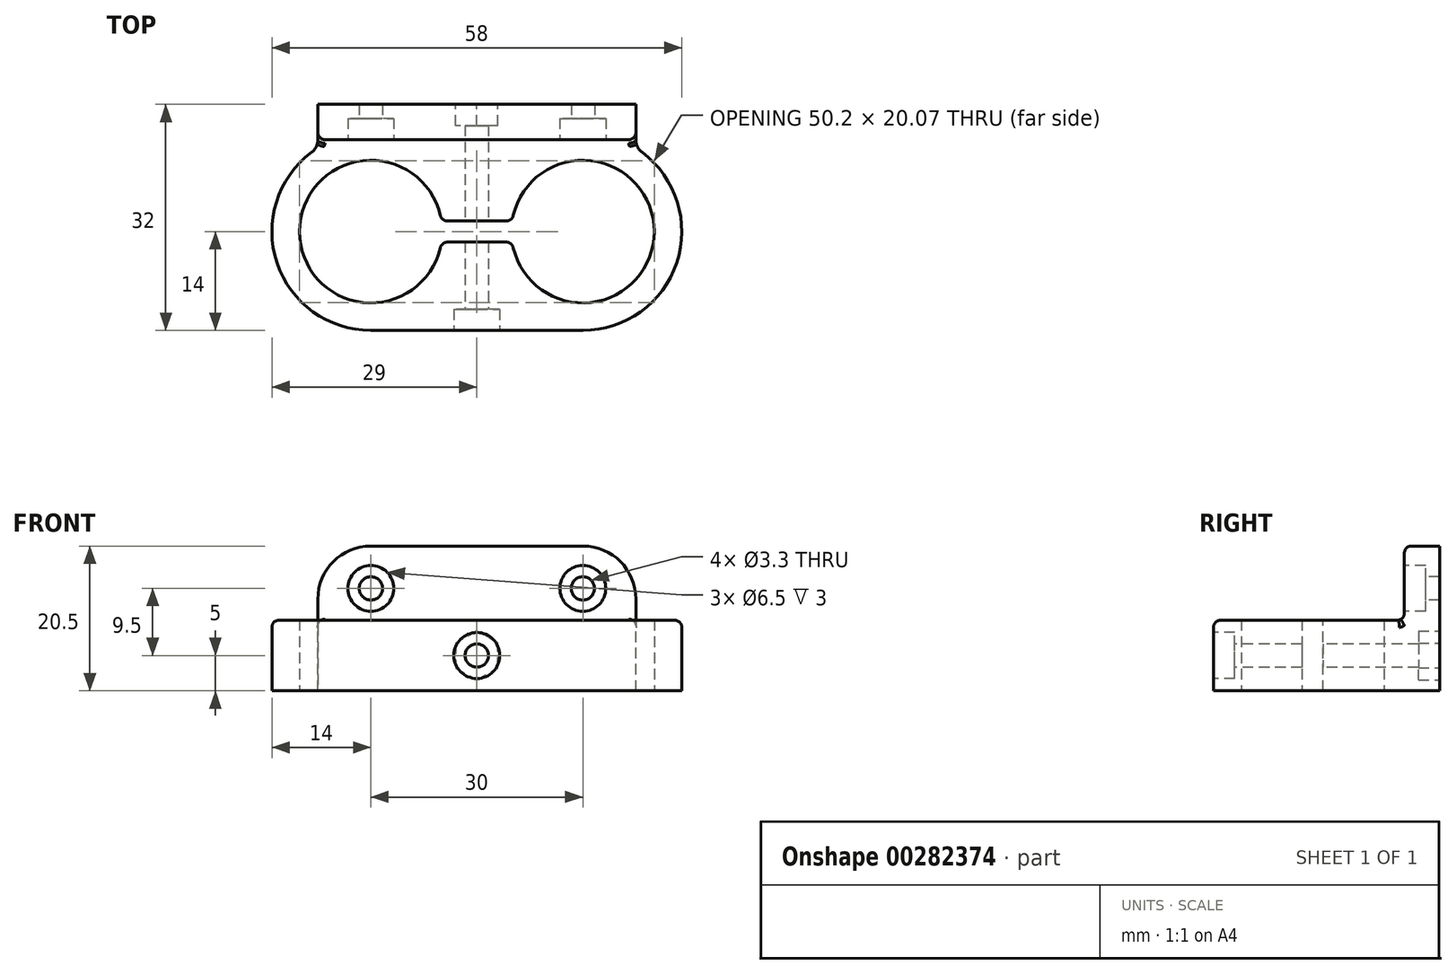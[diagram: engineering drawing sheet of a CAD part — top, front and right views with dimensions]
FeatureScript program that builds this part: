
annotation { "Feature Type Name" : "Feature", "Feature Type Description" : "" }
export const myFeature = defineFeature(function(context is Context, id is Id, definition is map)
    precondition{}
    {
        {
            var Q0;
            Q0=qCreatedBy(makeId("Front.planeOp"),FACE);
            var sketch = newSketch(context, id + "F0", { "sketchPlane" : qUnion([Q0])});
            skLineSegment(sketch, "E0.bottom", {"start": v(0, 0) * mm, "end": v(45, 0) * mm});
            skLineSegment(sketch, "E0.top", {"start": v(7.5, 20.5) * mm, "end": v(37.5, 20.5) * mm});
            skLineSegment(sketch, "E0.left", {"start": v(0, 0) * mm, "end": v(0, 13) * mm});
            skLineSegment(sketch, "E0.right", {"start": v(45, 0) * mm, "end": v(45, 13) * mm});
            skPoint(sketch, "E1.visualSharp", {"position": v(0, 20.5) * mm});
            skArc(sketch, "E1.filletArc", {"start": v(7.5, 20.5) * mm, "mid": v(2.2, 18.3) * mm, "end": v(0, 13) * mm});
            skPoint(sketch, "E2.visualSharp", {"position": v(45, 20.5) * mm});
            skArc(sketch, "E2.filletArc", {"start": v(45, 13) * mm, "mid": v(42.8, 18.3) * mm, "end": v(37.5, 20.5) * mm});
            skSolve(sketch);
        }
        {
            var Q0;
            Q0=qSketchRegion(id+"F0",true);
            extrude(context, id + "F1", {"entities" : qUnion([Q0]), "depth" : 5 * mm});
        }
        {
            var Q0;
            Q0=makeQuery(id+"F1.opExtrude","CAP_FACE",FACE,{"disambiguationData":[OSD([sQuery(id+"F0.wireOp",EDGE,"E0.bottom"),sQuery(id+"F0.wireOp",EDGE,"E0.top"),sQuery(id+"F0.wireOp",EDGE,"E0.left"),sQuery(id+"F0.wireOp",EDGE,"E0.right")])],"isStart":false});
            var sketch = newSketch(context, id + "F2", { "sketchPlane" : qUnion([Q0])});
            skLineSegment(sketch, "E3", {"start": v(0, 14.5) * mm, "end": v(45, 14.5) * mm, "construction": true});
            skLineSegment(sketch, "E4", {"start": v(22.5, 20.5) * mm, "end": v(22.5, 14.5) * mm, "construction": true});
            skPoint(sketch, "E5", {"position": v(7.5, 14.5) * mm});
            skPoint(sketch, "E6", {"position": v(37.5, 14.5) * mm});
            skSolve(sketch);
        }
        {
            var Q0;
            Q0=sQuery(id+"F2.wireOp",VERTEX,"E5");
            var Q1;
            Q1=sQuery(id+"F2.wireOp",VERTEX,"E6");
            var Q2;
            Q2=makeQuery(id+"F1.opExtrude","SWEPT_BODY",BODY,{"disambiguationData":[OSD([sQuery(id+"F0.wireOp",EDGE,"E0.bottom"),sQuery(id+"F0.wireOp",EDGE,"E0.top"),sQuery(id+"F0.wireOp",EDGE,"E0.left"),sQuery(id+"F0.wireOp",EDGE,"E0.right")])]});
            hole(context, id + "F3", {"style" : HoleStyle.C_BORE, "endStyle" : HoleEndStyle.THROUGH, "standardTappedOrClearance" : lookupTablePath({ "standard" : "ISO", "fit" : "Normal", "size" : "M3", "type" : "Clearance" }), "standardBlindInLast" : lookupTablePath({ "fit" : "Standard", "standard" : "ISO", "size" : "M3", "type" : "Clearance" }), "holeDiameter" : 3.3 * mm, "cBoreDiameter" : 6.5 * mm, "cBoreDepth" : 3 * mm, "tappedDepth" : 3 * mm, "tapClearance" : 3, "startFromSketch" : true, "locations" : qUnion([Q0, Q1]), "scope" : qUnion([Q2])});
        }
        {
            var Q0;
            Q0=qCreatedBy(makeId("Top.planeOp"),FACE);
            var sketch = newSketch(context, id + "F4", { "sketchPlane" : qUnion([Q0])});
            skLineSegment(sketch, "E7.bottom", {"start": v(0, 0) * mm, "end": v(45, 0) * mm});
            skLineSegment(sketch, "E7.top", {"start": v(7.5, -32) * mm, "end": v(37.5, -32) * mm});
            skLineSegment(sketch, "E7.left", {"start": v(0, 0) * mm, "end": v(0, -6.18) * mm});
            skLineSegment(sketch, "E7.right", {"start": v(45, 0) * mm, "end": v(45, -6.18) * mm});
            skLineSegment(sketch, "E8", {"start": v(0, -18) * mm, "end": v(45, -18) * mm, "construction": true});
            skLineSegment(sketch, "E9", {"start": v(22.5, -18) * mm, "end": v(22.5, -32) * mm, "construction": true});
            skArc(sketch, "E10", {"start": v(17.49, -16.5) * mm, "mid": v(-2.6, -18) * mm, "end": v(17.49, -19.5) * mm});
            skArc(sketch, "E11", {"start": v(27.51, -19.5) * mm, "mid": v(47.6, -18) * mm, "end": v(27.51, -16.5) * mm});
            skArc(sketch, "E12", {"start": v(37.5, -32) * mm, "mid": v(50.94, -21.9) * mm, "end": v(45, -6.18) * mm});
            skArc(sketch, "E13", {"start": v(0, -6.18) * mm, "mid": v(-5.94, -21.9) * mm, "end": v(7.5, -32) * mm});
            skLineSegment(sketch, "E14.trimOffspring", {"start": v(0, -18) * mm, "end": v(0, -32) * mm, "construction": true});
            skLineSegment(sketch, "E15.trimOffspring", {"start": v(45, -18) * mm, "end": v(45, -32) * mm, "construction": true});
            skLineSegment(sketch, "E16.0", {"start": v(17.49, -19.5) * mm, "end": v(27.51, -19.5) * mm});
            skLineSegment(sketch, "E17.0", {"start": v(17.49, -16.5) * mm, "end": v(27.51, -16.5) * mm});
            skSolve(sketch);
        }
        {
            var Q0;
            Q0=qSketchRegion(id+"F4",true);
            extrude(context, id + "F5", {"entities" : qUnion([Q0]), "operationType" : NewBodyOperationType.ADD, "depth" : 10 * mm});
        }
        {
            var Q0;
            Q0=makeQuery(id+"F5.opExtrude","SWEPT_FACE",FACE,{"disambiguationData":[OSD([sQuery(id+"F4.wireOp",EDGE,"E7.top")])]});
            var sketch = newSketch(context, id + "F6", { "sketchPlane" : qUnion([Q0])});
            skLineSegment(sketch, "E18", {"start": v(7.5, 5) * mm, "end": v(37.5, 5) * mm, "construction": true});
            skPoint(sketch, "E19", {"position": v(22.5, 5) * mm});
            skSolve(sketch);
        }
        {
            var Q0;
            Q0=sQuery(id+"F6.wireOp",VERTEX,"E19");
            var Q1;
            Q1=makeQuery(id+"F1.opExtrude","SWEPT_BODY",BODY,{"disambiguationData":[OSD([sQuery(id+"F0.wireOp",EDGE,"E0.bottom"),sQuery(id+"F0.wireOp",EDGE,"E0.top"),sQuery(id+"F0.wireOp",EDGE,"E0.left"),sQuery(id+"F0.wireOp",EDGE,"E0.right"),sQuery(id+"F0.wireOp",EDGE,"E1.filletArc"),sQuery(id+"F0.wireOp",EDGE,"E2.filletArc")])]});
            hole(context, id + "F7", {"style" : HoleStyle.C_BORE, "endStyle" : HoleEndStyle.THROUGH, "standardTappedOrClearance" : lookupTablePath({ "standard" : "ISO", "fit" : "Normal", "size" : "M3", "type" : "Clearance" }), "standardBlindInLast" : lookupTablePath({ "fit" : "Standard", "standard" : "ISO", "size" : "M3", "type" : "Clearance" }), "holeDiameter" : 3.3 * mm, "cBoreDiameter" : 6.5 * mm, "cBoreDepth" : 3 * mm, "tappedDepth" : 3 * mm, "tapClearance" : 3, "startFromSketch" : true, "locations" : qUnion([Q0]), "scope" : qUnion([Q1])});
        }
        {
            var Q0;
            Q0=makeQuery(id+"F1.opExtrude","CAP_FACE",FACE,{"disambiguationData":[OSD([sQuery(id+"F0.wireOp",EDGE,"E0.bottom"),sQuery(id+"F0.wireOp",EDGE,"E0.top"),sQuery(id+"F0.wireOp",EDGE,"E0.left"),sQuery(id+"F0.wireOp",EDGE,"E0.right"),sQuery(id+"F0.wireOp",EDGE,"E1.filletArc"),sQuery(id+"F0.wireOp",EDGE,"E2.filletArc")])],"isStart":true});
            var sketch = newSketch(context, id + "F8", { "sketchPlane" : qUnion([Q0])});
            skCircle(sketch, "E20.cCircle", {"center": v(-22.5, 5) * mm, "radius": 3 * mm, "construction": true});
            skLineSegment(sketch, "E20.0", {"start": v(-19.5, 6.73) * mm, "end": v(-19.5, 3.27) * mm});
            skLineSegment(sketch, "E20.1", {"start": v(-19.5, 3.27) * mm, "end": v(-22.5, 1.54) * mm});
            skLineSegment(sketch, "E20.2", {"start": v(-22.5, 1.54) * mm, "end": v(-25.5, 3.27) * mm});
            skLineSegment(sketch, "E20.3", {"start": v(-25.5, 3.27) * mm, "end": v(-25.5, 6.73) * mm});
            skLineSegment(sketch, "E20.4", {"start": v(-25.5, 6.73) * mm, "end": v(-22.5, 8.46) * mm});
            skLineSegment(sketch, "E20.5", {"start": v(-22.5, 8.46) * mm, "end": v(-19.5, 6.73) * mm});
            skPoint(sketch, "E20.0.midPoint", {"position": v(-19.5, 5) * mm});
            skSolve(sketch);
        }
        {
            var Q0;
            Q0=qSketchRegion(id+"F8",true);
            extrude(context, id + "F9", {"entities" : qUnion([Q0]), "operationType" : NewBodyOperationType.REMOVE, "oppositeDirection" : true, "depth" : 3 * mm});
        }
        {
            var Q0;
            Q0=makeQuery(id+"F5.opExtrude","SWEPT_EDGE",EDGE,{"disambiguationData":[OSD([sQuery(id+"F4.wireOp",EDGE,"E7.right"),sQuery(id+"F4.wireOp",EDGE,"E12")])]});
            var Q1;
            Q1=makeQuery(id+"F5.opExtrude","SWEPT_EDGE",EDGE,{"disambiguationData":[OSD([sQuery(id+"F4.wireOp",EDGE,"E7.left"),sQuery(id+"F4.wireOp",EDGE,"E13")])]});
            fillet(context, id + "F10", {"entities" : qUnion([Q0, Q1]), "radius" : 2.25 * mm, "tangentPropagation" : true, "allowEdgeOverflow" : false});
        }
        {
            var Q0;
            Q0=makeQuery(id+"F5.boolean.opBoolean","INTERSECT",EDGE,{"derivedFrom":[makeQuery(id+"F1.opExtrude","CAP_FACE",FACE,{"disambiguationData":[OSD([sQuery(id+"F0.wireOp",EDGE,"E0.bottom"),sQuery(id+"F0.wireOp",EDGE,"E0.top"),sQuery(id+"F0.wireOp",EDGE,"E0.left"),sQuery(id+"F0.wireOp",EDGE,"E0.right"),sQuery(id+"F0.wireOp",EDGE,"E1.filletArc"),sQuery(id+"F0.wireOp",EDGE,"E2.filletArc")])],"isStart":false}),makeQuery(id+"F5.opExtrude","CAP_FACE",FACE,{"disambiguationData":[OSD([sQuery(id+"F4.wireOp",EDGE,"E7.bottom"),sQuery(id+"F4.wireOp",EDGE,"E7.top"),sQuery(id+"F4.wireOp",EDGE,"E7.left"),sQuery(id+"F4.wireOp",EDGE,"E7.right"),sQuery(id+"F4.wireOp",EDGE,"E10"),sQuery(id+"F4.wireOp",EDGE,"E11"),sQuery(id+"F4.wireOp",EDGE,"E12"),sQuery(id+"F4.wireOp",EDGE,"E13"),sQuery(id+"F4.wireOp",EDGE,"E16.0"),sQuery(id+"F4.wireOp",EDGE,"E17.0")])],"isStart":false})]});
            fillet(context, id + "F11", {"entities" : qUnion([Q0]), "radius" : 1 * mm, "tangentPropagation" : true, "allowEdgeOverflow" : false});
        }
        {
            var Q0;
            Q0=makeQuery(id+"F5.opExtrude","CAP_EDGE",EDGE,{"disambiguationData":[OSD([sQuery(id+"F4.wireOp",EDGE,"E7.top")])],"isStart":false});
            var Q1;
            Q1=makeQuery(id+"F5.opExtrude","SWEPT_EDGE",EDGE,{"disambiguationData":[OSD([sQuery(id+"F4.wireOp",EDGE,"E11"),sQuery(id+"F4.wireOp",EDGE,"E17.0")])]});
            var Q2;
            Q2=makeQuery(id+"F5.opExtrude","SWEPT_EDGE",EDGE,{"disambiguationData":[OSD([sQuery(id+"F4.wireOp",EDGE,"E11"),sQuery(id+"F4.wireOp",EDGE,"E16.0")])]});
            var Q3;
            Q3=makeQuery(id+"F5.opExtrude","SWEPT_EDGE",EDGE,{"disambiguationData":[OSD([sQuery(id+"F4.wireOp",EDGE,"E10"),sQuery(id+"F4.wireOp",EDGE,"E17.0")])]});
            var Q4;
            Q4=makeQuery(id+"F5.opExtrude","SWEPT_EDGE",EDGE,{"disambiguationData":[OSD([sQuery(id+"F4.wireOp",EDGE,"E10"),sQuery(id+"F4.wireOp",EDGE,"E16.0")])]});
            fillet(context, id + "F12", {"entities" : qUnion([Q0, Q1, Q2, Q3, Q4]), "radius" : 1 * mm, "tangentPropagation" : true, "allowEdgeOverflow" : false});
        }
    });
